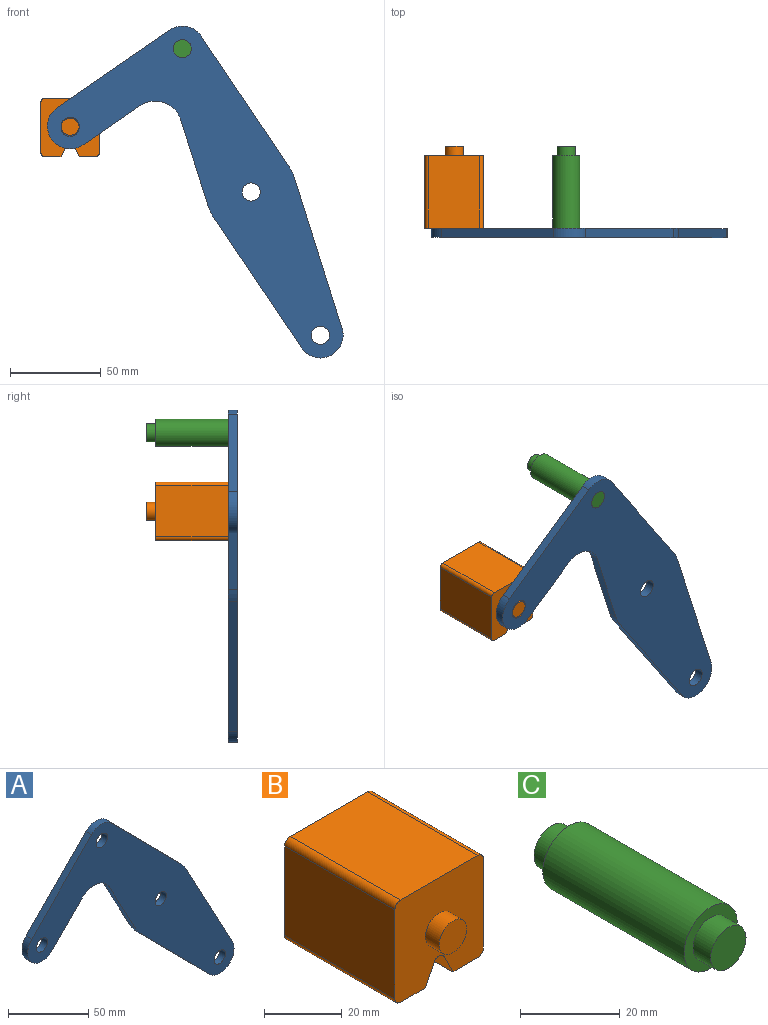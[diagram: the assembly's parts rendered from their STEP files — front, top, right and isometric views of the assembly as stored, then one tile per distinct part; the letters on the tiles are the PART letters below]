
ASSEMBLY  parts=3 mates=1
PART A: 18 faces, bbox 181.7x5x165.8 mm
  f0: plane 43.49x23.35mm, normal (-0.88,0,-0.47), area 246.8mm2, adj f1,f14,f16,f17
  f1: cylinder r=25mm len=5.75mm, axis (0,1,0), area 35.8mm2, adj f0,f2,f16,f17
  f2: plane 61.6x60.87mm, normal (-0.71,0,-0.7), area 433mm2, adj f1,f3,f16,f17
  f3: cylinder r=12.5mm len=21.39mm, axis (0,1,0), area 178.4mm2, adj f2,f4,f16,f17
  f4: plane 76.3x40.96mm, normal (0.88,0,0.47), area 433mm2, adj f3,f5,f16,f17
  f5: cylinder r=25mm len=5.75mm, axis (0,1,0), area 35.8mm2, adj f4,f6,f16,f17
  f6: plane 61.6x60.87mm, normal (0.71,0,0.7), area 433mm2, adj f5,f7,f16,f17
  f7: cylinder r=12.5mm len=17.78mm, axis (0,1,0), area 98.9mm2, adj f6,f8,f16,f17
  f8: plane 53.35x52.71mm, normal (-0.71,0,0.7), area 375mm2, adj f7,f9,f16,f17
  f9: cylinder r=12.5mm len=21.39mm, axis (0,1,0), area 196.3mm2, adj f8,f10,f16,f17
  f10: plane 26.86x26.54mm, normal (0.71,0,-0.7), area 188.8mm2, adj f9,f14,f16,f17
  f11: cylinder r=5mm len=10mm, axis (0,1,0), area 157.1mm2, adj f16,f17
  f12: cylinder r=5mm len=10mm, axis (0,1,0), area 157.1mm2, adj f16,f17
  f13: cylinder r=5mm len=10mm, axis (0,1,0), area 157.1mm2, adj f16,f17
  f14: cylinder r=15mm len=23.89mm, axis (0,1,0), area 140.2mm2, adj f0,f10,f16,f17
  f15: cylinder r=5mm len=10mm, axis (0,1,0), area 157.1mm2, adj f16,f17
  f16: plane 181.66x165.78mm, normal (0,-1,0), area 8710.1mm2, adj f0,f1,f2,f3,f4,f5,f6,f7
  f17: plane 181.66x165.78mm, normal (0,1,0), area 8710.1mm2, adj f0,f1,f2,f3,f4,f5,f6,f7
PART B: 18 faces, bbox 32.1x50x32.1 mm
  f0: plane 40x28.08mm, normal (1,0,0), area 1123.1mm2, adj f4,f10,f13,f14
  f1: plane 40x9.04mm, normal (0,0,-1), area 361.6mm2, adj f2,f4,f10,f14
  f2: plane 40x6.42mm, normal (-0.89,0,-0.45), area 287.2mm2, adj f1,f4,f10,f15
  f3: plane 40x6.42mm, normal (0.89,0,-0.45), area 287.2mm2, adj f4,f5,f10,f15
  f4: plane 32.08x32.08mm, normal (0,-1,0), area 900.6mm2, adj f0,f1,f2,f3,f5,f6,f7,f9
  f5: plane 40x9.04mm, normal (0,0,-1), area 361.6mm2, adj f3,f4,f10,f16
  f6: plane 40x28.08mm, normal (0,0,1), area 1123.1mm2, adj f4,f10,f13,f17
  f7: plane 40x28.08mm, normal (-1,0,0), area 1123.1mm2, adj f4,f10,f16,f17
  f8: plane 10x10mm, normal (0,-1,0), area 78.5mm2, adj f9
  f9: cylinder r=5mm len=10mm, axis (0,1,0), area 157.1mm2, adj f4,f8
  f10: plane 32.08x32.08mm, normal (0,1,0), area 900.6mm2, adj f0,f1,f2,f3,f5,f6,f7,f12
  f11: plane 10x10mm, normal (0,1,0), area 78.5mm2, adj f12
  f12: cylinder r=5mm len=10mm, axis (0,-1,0), area 157.1mm2, adj f10,f11
  f13: cylinder r=2mm len=40mm, axis (0,1,0), area 125.7mm2, adj f0,f4,f6,f10
  f14: cylinder r=2mm len=40mm, axis (0,-1,0), area 125.7mm2, adj f0,f1,f4,f10
  f15: cylinder r=2mm len=40mm, axis (0,1,0), area 177.1mm2, adj f2,f3,f4,f10
  f16: cylinder r=2mm len=40mm, axis (0,1,0), area 125.7mm2, adj f4,f5,f7,f10
  f17: cylinder r=2mm len=40mm, axis (0,-1,0), area 125.7mm2, adj f4,f6,f7,f10
PART C: 7 faces, bbox 15x50x15 mm
  f0: cylinder r=7.5mm len=40mm, axis (0,-1,0), area 1885mm2, adj f2,f5
  f1: cylinder r=5mm len=10mm, axis (0,1,0), area 157.1mm2, adj f2,f3
  f2: plane 15x15mm, normal (0,-1,0), area 98.2mm2, adj f0,f1
  f3: plane 10x10mm, normal (0,-1,0), area 78.5mm2, adj f1
  f4: cylinder r=5mm len=10mm, axis (0,-1,0), area 157.1mm2, adj f5,f6
  f5: plane 15x15mm, normal (0,1,0), area 98.2mm2, adj f0,f4
  f6: plane 10x10mm, normal (0,1,0), area 78.5mm2, adj f4
PLACE A rot(axis=(0,1,0),10.7deg) t=(0,-20,0)mm fixed
PLACE B t=(4.99,-20,18.49)mm
PLACE C rot(axis=(0,1,0),10.7deg) t=(0,-20,0)mm
MATE revolute B.f4 <-> A.f9  axis (0,-1,0) through (-99.69,-20,36.21)mm
